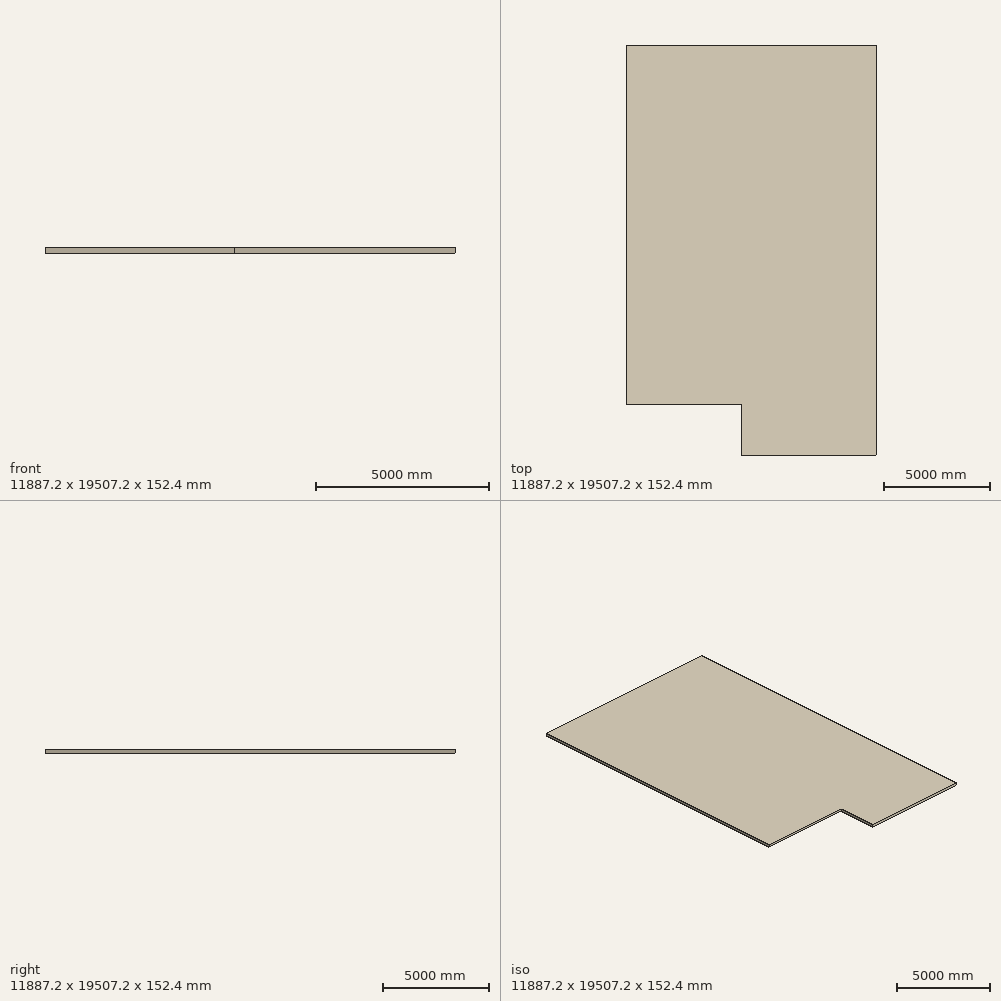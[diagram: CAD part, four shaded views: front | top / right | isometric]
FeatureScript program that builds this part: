
annotation { "Feature Type Name" : "Feature", "Feature Type Description" : "" }
export const myFeature = defineFeature(function(context is Context, id is Id, definition is map)
    precondition{}
    {
        {
            var Q0;
            Q0=qCreatedBy(makeId("Top.planeOp"),FACE);
            var sketch = newSketch(context, id + "F0", { "sketchPlane" : qUnion([Q0])});
            skLineSegment(sketch, "E0.bottom", {"start": v(-457.2, -8534.4) * mm, "end": v(-5943.6, -8534.4) * mm});
            skLineSegment(sketch, "E0.top", {"start": v(5943.6, 8534.4) * mm, "end": v(-5943.6, 8534.4) * mm});
            skLineSegment(sketch, "E0.left", {"start": v(5943.6, -10972.8) * mm, "end": v(5943.6, 8534.4) * mm});
            skLineSegment(sketch, "E0.right", {"start": v(-5943.6, -8534.4) * mm, "end": v(-5943.6, 8534.4) * mm});
            skPoint(sketch, "E0.middle", {"position": v(0, 0) * mm});
            skLineSegment(sketch, "E1", {"start": v(-457.2, -8534.4) * mm, "end": v(-457.2, -10972.8) * mm});
            skLineSegment(sketch, "E2", {"start": v(-457.2, -10972.8) * mm, "end": v(5943.6, -10972.8) * mm});
            skPoint(sketch, "E3.orphan", {"position": v(5943.6, -8534.4) * mm});
            skSolve(sketch);
        }
        {
            var Q0;
            Q0=makeQuery(id+"F0.imprint","IMPRINT",FACE,{"disambiguationData":[TD([[makeQuery(id+"F0.imprint","IMPRINT",EDGE,{"derivedFrom":sQuery(id+"F0.wireOp",EDGE,"E0.bottom")}),-1.0]])]});
            extrude(context, id + "F1", {"entities" : qUnion([Q0]), "depth" : 152.4 * mm});
        }
    });
